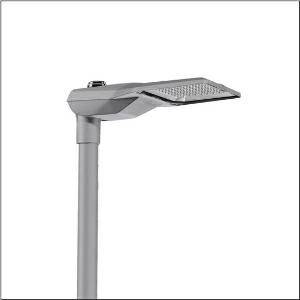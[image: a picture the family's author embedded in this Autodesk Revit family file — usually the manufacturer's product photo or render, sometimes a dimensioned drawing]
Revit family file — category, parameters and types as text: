
# Revit family: streetlight_sl_21_midi___pl52_5xe7h37n08lb_6d16
name_source: partatom
category: Lighting Fixtures
units: mm (PartAtom-declared; Revit-internal decimal feet)

## family parameters
Cut with Voids When Loaded = No
Host = Face
Light Source = No
Part Type = Normal
Room Calculation Point = No
Round Connector Dimension = Use Diameter
Shared = No

## types (1)
- --- (1 x LED, 14100 lm, 98.3 W, 3000K)
    Apparent Load = 98 VA
    CIE Flux Codes = 27 59 98 100 100
    Color Rendering = 70
    Color Temperature = 3000K
    Default Elevation = 1800 mm
    Description = Streetlight SL 21 midi, mast luminaire, primary light control with lens, of PMMA, primary optical cover: cover, of toughened safety glass, transparent, light distribution: PL52, light emission: direct distribution, primary light characteristic: asymmetric, installation type: side-entry, LED, 3G 2.5mm², High Power LED, rated luminous flux: 14.100lm, luminous efficacy: 143lm/W, light colour: 730, colour temperature: 3000K, control: overheat protection, presetting dimming linear, constant luminous flux control, time-dependent luminous flux control, flexible luminous flux parameterisation, mains connection: 220..240V, AC, 50/60Hz, connection cable pre-assembled, cable length: 10,5m, wiring characteristics: H05VV-F, start of lifetime: 98W, end of service life: 101W, reduction: 45W, luminaire housing, of diecast aluminium (EN AC-44300), powder-coated, Siteco® metallic grey (DB 702S), corrosivity category C5 mid according to DIN EN ISO 12944, multi-level sealing system, sealing non-destructively replaceable, inclination adjustable: 0°, 5°, 10°, 15°, length: 644mm, width: 335mm, height: 110mm, spigot size: 42mm (side-entry), protection rating (complete): IP66, insulation class (complete): insulation class I (protective earthing), certification: CE, ENEC, ENEC+, VDE, impact resistance: IK09, permissible operating ambient temperature for outdoor applications: -40..+50°C, standard-compliant lighting for roads and squares, packaging unit: 1 piece

Light Distribution: PL52
    Height = 111 mm
    Lamp = 1 x LED
    Lamp Light Flux = 14100 lm
    Lamp Power = 98.3 W
    Lamp count = 1
    Length = 644 mm
    Luminous efficacy = 143 lm/W
    Manufacturer = Siteco
    ModVariant = No
    Model = 5XE7H37N08LB
    Number of Poles = 1
    OnlyDefault = Yes
    Power Factor = 1
    Product Name = Streetlight SL 21 midi | PL52
    Product group = mast luminaire | pylon top
    ProductGroupID = 6100
    Protection Class = Protection class I
    Protection Degree = IP 66
    RLX_Detail_Level = 1
    RLX_Emergency_Light_Flux = 0 lm
    RLX_Emergency_Type = 0
    RLX_Emergency_Type_DB = No
    RlxData = <blob elided: 100197 chars, md5=161695c7>
    Socket = socket
    Standby Power = 0 W
    System Light Flux = 14100 lm
    System Power = 98 W
    Type Comments = factory setting: luminous flux: 100 % | dim-lin: 254 | 1020 mA
    Type Image = l_1294377.jpg
    URL = http://relux.com
    VarID = @adj_068259
    Voltage = 0 V
    Weight = 0.00 kg
    Width = 336 mm

## geometry (parser evidence)
native form markers: Blend x4, Sweep x9
no freeform markers — native parametric forms only
